# Revit family: STL22455BR_STL22455PTO
name_source: partatom
category: Luminárias
units: mm (PartAtom-declared; Revit-internal decimal feet)

## family parameters
Com base no plano de trabalho = Não
Compartilhado = Não
Corte com vazios quando carregada = Não
Cota do conector redondo = Utilizar diâmetro
Fonte luminosa = Não
Manter orientação da anotação = Não
Número OmniClass = 23.80.70.00
Ponto de cálculo do ambiente = Não
Sempre na vertical = Sim
Tipo de parte = Normal
Título OmniClass = Lighting

## types (2) — shared parameters
Acabamento Spot = Al - Preto
Fabricante = Stella
Grau de proteção (IP) = IP20
Modelo = Flow PAR30 CDMR para Trace
Tensão Elétrica = 127-220V
URL = https://stella.com.br
zero-valued in all types: Altura do Spot, Comprimento do Spot, Diâmetro do Spot, Elevação padrão

## per-type parameters (varying)
| type | Estrutura | Potência máxima | Referência |
| STL22455BR - BRANCO | Al - Branco | 20 W | STL22455BR |
| STL22455PTO - PRETO | Al - Preto | 15 W | STL22455PTO |
